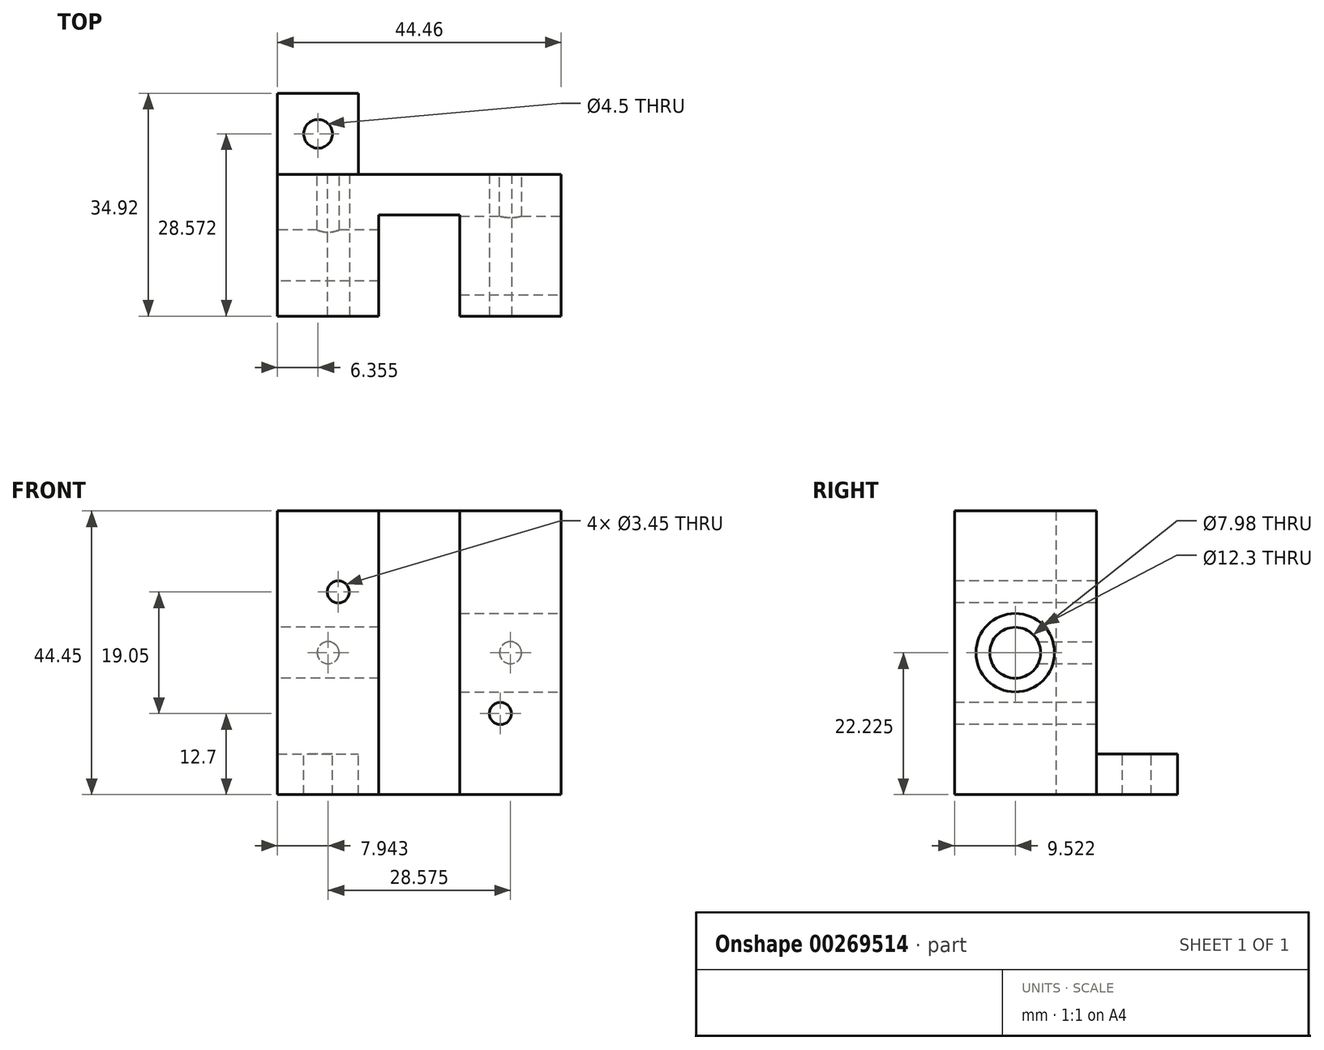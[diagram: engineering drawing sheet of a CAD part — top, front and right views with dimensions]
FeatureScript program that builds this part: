
annotation { "Feature Type Name" : "Feature", "Feature Type Description" : "" }
export const myFeature = defineFeature(function(context is Context, id is Id, definition is map)
    precondition{}
    {
        {
            var Q0;
            Q0=qCreatedBy(makeId("Top.planeOp"),FACE);
            var sketch = newSketch(context, id + "F0", { "sketchPlane" : qUnion([Q0])});
            skLineSegment(sketch, "E0.bottom", {"start": v(22.23, -11.11) * mm, "end": v(-22.22, -11.11) * mm});
            skLineSegment(sketch, "E0.top", {"start": v(22.23, 11.11) * mm, "end": v(-22.23, 11.11) * mm});
            skLineSegment(sketch, "E0.left", {"start": v(22.23, -11.11) * mm, "end": v(22.23, 11.11) * mm});
            skLineSegment(sketch, "E0.right", {"start": v(-22.22, -11.11) * mm, "end": v(-22.23, 11.11) * mm});
            skPoint(sketch, "E0.middle", {"position": v(0, 0) * mm});
            skSolve(sketch);
        }
        {
            var Q0;
            Q0=qSketchRegion(id+"F0",true);
            extrude(context, id + "F1", {"entities" : qUnion([Q0]), "depth" : 44.45 * mm});
        }
        {
            var Q0;
            Q0=makeQuery(id+"F1.opExtrude","SWEPT_FACE",FACE,{"disambiguationData":[OSD([sQuery(id+"F0.wireOp",EDGE,"E0.bottom")])]});
            var sketch = newSketch(context, id + "F2", { "sketchPlane" : qUnion([Q0])});
            skLineSegment(sketch, "E1.bottom", {"start": v(6.35, 44.45) * mm, "end": v(-6.35, 44.45) * mm});
            skLineSegment(sketch, "E1.top", {"start": v(6.35, 0) * mm, "end": v(-6.35, 0) * mm});
            skLineSegment(sketch, "E1.left", {"start": v(6.35, 44.45) * mm, "end": v(6.35, 0) * mm});
            skLineSegment(sketch, "E1.right", {"start": v(-6.35, 44.45) * mm, "end": v(-6.35, 0) * mm});
            skPoint(sketch, "E1.middle", {"position": v(0, 22.23) * mm});
            skSolve(sketch);
        }
        {
            var Q0;
            Q0=qSketchRegion(id+"F2",true);
            extrude(context, id + "F3", {"entities" : qUnion([Q0]), "operationType" : NewBodyOperationType.REMOVE, "oppositeDirection" : true, "depth" : 15.88 * mm});
        }
        {
            var Q0;
            {var subQ0=sQuery(id+"F0.wireOp",EDGE,"E0.right");var subQ3=sQuery(id+"F0.wireOp",EDGE,"E0.bottom");Q0=makeQuery(id+"F3.boolean.opBoolean","SPLIT",FACE,{"disambiguationData":[TD([makeQuery(id+"F1.opExtrude","SWEPT_FACE",FACE,{"disambiguationData":[OSD([subQ0])]})])],"derivedFrom":makeQuery(id+"F1.opExtrude","SWEPT_FACE",FACE,{"disambiguationData":[OSD([subQ3])]})});}
            var sketch = newSketch(context, id + "F4", { "sketchPlane" : qUnion([Q0])});
            skPoint(sketch, "E2", {"position": v(0, 22.23) * mm});
            skPoint(sketch, "E2.positionSnap0", {"position": v(-22.22, 22.23) * mm});
            skSolve(sketch);
        }
        {
            var Q0;
            {var subQ2=sQuery(id+"F0.wireOp",EDGE,"E0.top");Q0=makeQuery(id+"FXgTw227xVCnMee_1.boolean.opBoolean","SPLIT",FACE,{"disambiguationData":[TD([makeQuery(id+"FXgTw227xVCnMee_1.opExtrude","SWEPT_FACE",FACE,{"disambiguationData":[OSD([sQuery(id+"FvhYNkOiCg4Ymqy_1.wireOp",EDGE,"o51gSBLn-AetB-UL49-WPIu-vC9d7O5uvW7y.bottom")])]})])],"derivedFrom":makeQuery(id+"F1.opExtrude","SWEPT_FACE",FACE,{"disambiguationData":[OSD([subQ2])]})});}
            var sketch = newSketch(context, id + "F5", { "sketchPlane" : qUnion([Q0])});
            skLineSegment(sketch, "E3.bottom", {"start": v(22.23, 0) * mm, "end": v(9.52, 0) * mm});
            skLineSegment(sketch, "E3.top", {"start": v(22.23, 6.35) * mm, "end": v(9.52, 6.35) * mm});
            skLineSegment(sketch, "E3.left", {"start": v(22.23, 0) * mm, "end": v(22.23, 6.35) * mm});
            skLineSegment(sketch, "E3.right", {"start": v(9.53, 0) * mm, "end": v(9.52, 6.35) * mm});
            skSolve(sketch);
        }
        {
            var Q0;
            Q0=qSketchRegion(id+"F5",true);
            extrude(context, id + "F6", {"entities" : qUnion([Q0]), "operationType" : NewBodyOperationType.ADD, "depth" : 12.7 * mm});
        }
        {
            var Q0;
            Q0=makeQuery(id+"F6.opExtrude","SWEPT_FACE",FACE,{"disambiguationData":[OSD([sQuery(id+"F5.wireOp",EDGE,"E3.top")])]});
            var sketch = newSketch(context, id + "F7", { "sketchPlane" : qUnion([Q0])});
            skPoint(sketch, "E4", {"position": v(-15.88, 17.46) * mm});
            skPoint(sketch, "E4.positionSnap0", {"position": v(-15.88, 23.81) * mm});
            skPoint(sketch, "E4.positionSnap1", {"position": v(-9.53, 17.46) * mm});
            skSolve(sketch);
        }
        {
            var Q0;
            Q0=sQuery(id+"F7.wireOp",VERTEX,"E4");
            var Q1;
            Q1=makeQuery(id+"F1.opExtrude","SWEPT_BODY",BODY,{"disambiguationData":[OSD([sQuery(id+"F0.wireOp",EDGE,"E0.bottom"),sQuery(id+"F0.wireOp",EDGE,"E0.top"),sQuery(id+"F0.wireOp",EDGE,"E0.left"),sQuery(id+"F0.wireOp",EDGE,"E0.right")])]});
            hole(context, id + "F8", {"style" : HoleStyle.SIMPLE, "endStyle" : HoleEndStyle.THROUGH, "standardTappedOrClearance" : lookupTablePath({ "standard" : "ANSI", "fit" : "Normal (ASME)", "size" : "#8", "type" : "Clearance" }), "standardBlindInLast" : lookupTablePath({ "fit" : "Free", "standard" : "ANSI", "size" : "#8", "type" : "Clearance" }), "holeDiameter" : 4.5 * mm, "tappedDepth" : 9.52 * mm, "tapClearance" : 3, "locations" : qUnion([Q0]), "scope" : qUnion([Q1])});
        }
        {
            var Q0;
            {var subQ0=sQuery(id+"F0.wireOp",EDGE,"E0.right");var subQ3=sQuery(id+"F0.wireOp",EDGE,"E0.bottom");Q0=makeQuery(id+"F3.boolean.opBoolean","SPLIT",FACE,{"disambiguationData":[TD([makeQuery(id+"F1.opExtrude","SWEPT_FACE",FACE,{"disambiguationData":[OSD([subQ0])]})])],"derivedFrom":makeQuery(id+"F1.opExtrude","SWEPT_FACE",FACE,{"disambiguationData":[OSD([subQ3])]})});}
            var sketch = newSketch(context, id + "F9", { "sketchPlane" : qUnion([Q0])});
            skLineSegment(sketch, "E5.bottom", {"start": v(12.7, 31.75) * mm, "end": v(-12.7, 31.75) * mm, "construction": true});
            skLineSegment(sketch, "E5.top", {"start": v(12.7, 12.7) * mm, "end": v(-12.7, 12.7) * mm, "construction": true});
            skLineSegment(sketch, "E5.left", {"start": v(12.7, 31.75) * mm, "end": v(12.7, 12.7) * mm, "construction": true});
            skLineSegment(sketch, "E5.right", {"start": v(-12.7, 31.75) * mm, "end": v(-12.7, 12.7) * mm, "construction": true});
            skPoint(sketch, "E5.middle", {"position": v(0, 22.23) * mm});
            skSolve(sketch);
        }
        {
            var Q0;
            Q0=sQuery(id+"F9.wireOp",VERTEX,"E5.right.start");
            var Q1;
            Q1=sQuery(id+"F9.wireOp",VERTEX,"E5.left.end");
            var Q2;
            Q2=makeQuery(id+"F1.opExtrude","SWEPT_BODY",BODY,{"disambiguationData":[OSD([sQuery(id+"F0.wireOp",EDGE,"E0.bottom"),sQuery(id+"F0.wireOp",EDGE,"E0.top"),sQuery(id+"F0.wireOp",EDGE,"E0.left"),sQuery(id+"F0.wireOp",EDGE,"E0.right")])]});
            hole(context, id + "F10", {"style" : HoleStyle.SIMPLE, "endStyle" : HoleEndStyle.THROUGH, "standardTappedOrClearance" : lookupTablePath({ "standard" : "ANSI", "engagement" : "75%", "pitch" : "32 tpi", "size" : "#8", "type" : "Tapped" }), "standardBlindInLast" : lookupTablePath({ "standard" : "ANSI", "engagement" : "75%", "pitch" : "32 tpi", "size" : "#8", "type" : "Tapped" }), "holeDiameter" : 3.45 * mm, "showTappedDepth" : true, "tappedDepth" : 10.16 * mm, "tapClearance" : 3, "locations" : qUnion([Q0, Q1]), "scope" : qUnion([Q2]), "majorDiameter" : 4.17 * mm});
        }
        {
            var Q0;
            {var subQ0=sQuery(id+"F2.wireOp",EDGE,"E1.right");var subQ1=sQuery(id+"F2.wireOp",EDGE,"E1.left");var subQ2=makeQuery(id+"F3.boolean.opBoolean","COPY",FACE,{"derivedFrom":makeQuery(id+"F3.opExtrude","CAP_FACE",FACE,{"disambiguationData":[OSD([sQuery(id+"F2.wireOp",EDGE,"E1.bottom"),sQuery(id+"F2.wireOp",EDGE,"E1.top"),subQ1,subQ0])],"isStart":false})});Q0=makeQuery(id+"Fe4ofOpqrksOA5r_1.hole-0.boolean.opBoolean","SPLIT",FACE,{"disambiguationData":[TD([makeQuery(id+"F1.opExtrude","CAP_FACE",FACE,{"disambiguationData":[OSD([sQuery(id+"F0.wireOp",EDGE,"E0.bottom"),sQuery(id+"F0.wireOp",EDGE,"E0.top"),sQuery(id+"F0.wireOp",EDGE,"E0.left"),sQuery(id+"F0.wireOp",EDGE,"E0.right")])],"isStart":false})])],"derivedFrom":subQ2});}
            cPlane(context, id + "F11", {"entities" : qUnion([Q0]), "cplaneType" : CPlaneType.OFFSET, "offset" : 6.35 * mm, "width" : 152.4 * mm, "height" : 152.4 * mm});
        }
        {
            var Q0;
            {var subQ0=sQuery(id+"F5.wireOp",EDGE,"E3.left");Q0=makeQuery(id+"FuC1fNPsjMsuzZb_1.1.F6.boolean.opBoolean","MERGE",FACE,{"derivedFrom":[makeQuery(id+"F6.boolean.opBoolean","MERGE",FACE,{"derivedFrom":[makeQuery(id+"F1.opExtrude","SWEPT_FACE",FACE,{"disambiguationData":[OSD([sQuery(id+"F0.wireOp",EDGE,"E0.right")])]}),makeQuery(id+"F6.opExtrude","SWEPT_FACE",FACE,{"disambiguationData":[OSD([subQ0])]})]}),makeQuery(id+"FuC1fNPsjMsuzZb_1.1.F6.opExtrude","SWEPT_FACE",FACE,{"disambiguationData":[OSD([subQ0])]})]});}
            var sketch = newSketch(context, id + "F12", { "sketchPlane" : qUnion([Q0])});
            skCircle(sketch, "E6", {"center": v(1.59, 22.22) * mm, "radius": 3.99 * mm});
            skLineSegment(sketch, "E7", {"start": v(-11.46, 22.22) * mm, "end": v(1.59, 22.22) * mm, "construction": true});
            skSolve(sketch);
        }
        {
            var Q0;
            Q0 = qSketchRegion(id + "F12", true);
            extrude(context, id + "F13", {"entities" : qUnion([Q0]), "operationType" : NewBodyOperationType.REMOVE, "endBound" : BoundingType.THROUGH_ALL, "oppositeDirection" : true, "depth" : 25.4 * mm});
        }
        {
            var Q0;
            {var subQ0=sQuery(id+"F5.wireOp",EDGE,"E3.left");Q0=makeQuery(id+"FuC1fNPsjMsuzZb_1.1.FjG1qGQSF2N8PoX_1.1.F6.boolean.opBoolean","MERGE",FACE,{"derivedFrom":[makeQuery(id+"FjG1qGQSF2N8PoX_1.1.F6.boolean.opBoolean","MERGE",FACE,{"derivedFrom":[makeQuery(id+"F1.opExtrude","SWEPT_FACE",FACE,{"disambiguationData":[OSD([sQuery(id+"F0.wireOp",EDGE,"E0.left")])]}),makeQuery(id+"FjG1qGQSF2N8PoX_1.1.F6.opExtrude","SWEPT_FACE",FACE,{"disambiguationData":[OSD([subQ0])]})]}),makeQuery(id+"FuC1fNPsjMsuzZb_1.1.FjG1qGQSF2N8PoX_1.1.F6.opExtrude","SWEPT_FACE",FACE,{"disambiguationData":[OSD([subQ0])]})]});}
            var sketch = newSketch(context, id + "F14", { "sketchPlane" : qUnion([Q0])});
            skCircle(sketch, "E8", {"center": v(-1.59, 22.22) * mm, "radius": 6.15 * mm});
            skSolve(sketch);
        }
        {
            var Q0;
            Q0=makeQuery(id+"F14.imprint","IMPRINT",FACE,{"disambiguationData":[TD([[makeQuery(id+"F14.imprint","IMPRINT",EDGE,{"derivedFrom":sQuery(id+"F14.wireOp",EDGE,"E8")}),1.0]])]});
            var Q1;
            Q1=sQuery(id+"F14.wireOp",EDGE,"E8");
            extrude(context, id + "F15", {"entities" : qUnion([Q0]), "operationType" : NewBodyOperationType.REMOVE, "surfaceEntities" : qUnion([Q1]), "endBound" : BoundingType.UP_TO_NEXT, "oppositeDirection" : true, "depth" : 25.4 * mm});
        }
        {
            var Q0;
            Q0=makeQuery(id+"F1.opExtrude","SWEPT_FACE",FACE,{"disambiguationData":[OSD([sQuery(id+"F0.wireOp",EDGE,"E0.top")])]});
            var sketch = newSketch(context, id + "F16", { "sketchPlane" : qUnion([Q0])});
            skLineSegment(sketch, "E9.0", {"start": v(22.23, 26.21) * mm, "end": v(22.23, 18.24) * mm, "construction": true});
            skLineSegment(sketch, "E9.1", {"start": v(-22.23, 16.07) * mm, "end": v(-22.23, 28.38) * mm, "construction": true});
            skLineSegment(sketch, "E10.0", {"start": v(-6.35, 44.45) * mm, "end": v(-6.35, 0) * mm, "construction": true});
            skLineSegment(sketch, "E10.1", {"start": v(6.35, 44.45) * mm, "end": v(6.35, 0) * mm, "construction": true});
            skLineSegment(sketch, "E11", {"start": v(-6.35, 22.23) * mm, "end": v(-22.23, 22.23) * mm, "construction": true});
            skLineSegment(sketch, "E12", {"start": v(6.35, 22.23) * mm, "end": v(22.23, 22.23) * mm, "construction": true});
            skPoint(sketch, "E13", {"position": v(-14.29, 22.23) * mm});
            skPoint(sketch, "E14", {"position": v(14.29, 22.23) * mm});
            skSolve(sketch);
        }
        {
            var Q0;
            Q0=sQuery(id+"F16.wireOp",VERTEX,"E13");
            var Q1;
            Q1=sQuery(id+"F16.wireOp",VERTEX,"E14");
            var Q2;
            Q2=makeQuery(id+"F1.opExtrude","SWEPT_BODY",BODY,{"disambiguationData":[OSD([sQuery(id+"F0.wireOp",EDGE,"E0.bottom"),sQuery(id+"F0.wireOp",EDGE,"E0.top"),sQuery(id+"F0.wireOp",EDGE,"E0.left"),sQuery(id+"F0.wireOp",EDGE,"E0.right")])]});
            hole(context, id + "F17", {"style" : HoleStyle.SIMPLE, "endStyle" : HoleEndStyle.BLIND, "standardTappedOrClearance" : lookupTablePath({ "standard" : "ANSI", "engagement" : "75%", "pitch" : "32 tpi", "size" : "#8", "type" : "Tapped" }), "standardBlindInLast" : lookupTablePath({ "standard" : "ANSI", "engagement" : "75%", "pitch" : "32 tpi", "size" : "#8", "type" : "Tapped" }), "holeDiameter" : 3.45 * mm, "showTappedDepth" : true, "holeDepth" : 12.7 * mm, "tappedDepth" : 10.32 * mm, "tapClearance" : 3, "locations" : qUnion([Q0, Q1]), "scope" : qUnion([Q2]), "majorDiameter" : 4.17 * mm});
        }
    });
